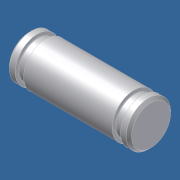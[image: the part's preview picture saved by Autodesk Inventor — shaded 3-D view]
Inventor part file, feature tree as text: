
AUTODESK INVENTOR PART (.ipt)
format: ipt  version: unknown  size: 210,432 bytes
history: native  units: in
note: dims shown in document units (in); Inventor stores cm internally (conversion verified against a paired STEP export)
features: other x49, revolve x1, sketch x1
ambient origin geometry x8: Origin, YZ Plane, XZ Plane, XY Plane, X Axis, Y Axis, Z Axis, Center Point
feature tree (51):
  revolve  "Revolution1"  [1 undecoded]
  other  "pin_XY"
  other  "pin_YZ"
  other  "pin_ZX"
  other  "pin_X"
  other  "pin_Y"
  other  "pin_Z"
  other  "pin_Center"
  other  "rr1_XY"
  other  "rr1_YZ"
  other  "rr1_ZX"
  other  "rr1_X"
  other  "rr1_Y"
  other  "rr1_Z"
  other  "rr1_Center"
  other  "rr2_XY"
  other  "rr2_YZ"
  other  "rr2_ZX"
  other  "rr2_X"
  other  "rr2_Y"
  other  "rr2_Z"
  other  "rr2_Center"
  other  "w21_XY"
  other  "w21_YZ"
  other  "w21_ZX"
  other  "w21_X"
  other  "w21_Y"
  other  "w21_Z"
  other  "w21_Center"
  other  "w22_XY"
  other  "w22_YZ"
  other  "w22_ZX"
  other  "w22_X"
  other  "w22_Y"
  other  "w22_Z"
  other  "w22_Center"
  other  "p1_XY"
  other  "p1_YZ"
  other  "p1_ZX"
  other  "p1_X"
  other  "p1_Y"
  other  "p1_Z"
  other  "p1_Center"
  other  "p2_XY"
  other  "p2_YZ"
  other  "p2_ZX"
  other  "p2_X"
  other  "p2_Y"
  other  "p2_Z"
  other  "p2_Center"
  sketch  "Sketch_1"  dims[d0=360.0deg]
note: 1 required parameter value undecoded (feature->parameter linkage not recoverable at this tier; creation-order binding heuristic only, values carry confidence <= 0.55)
